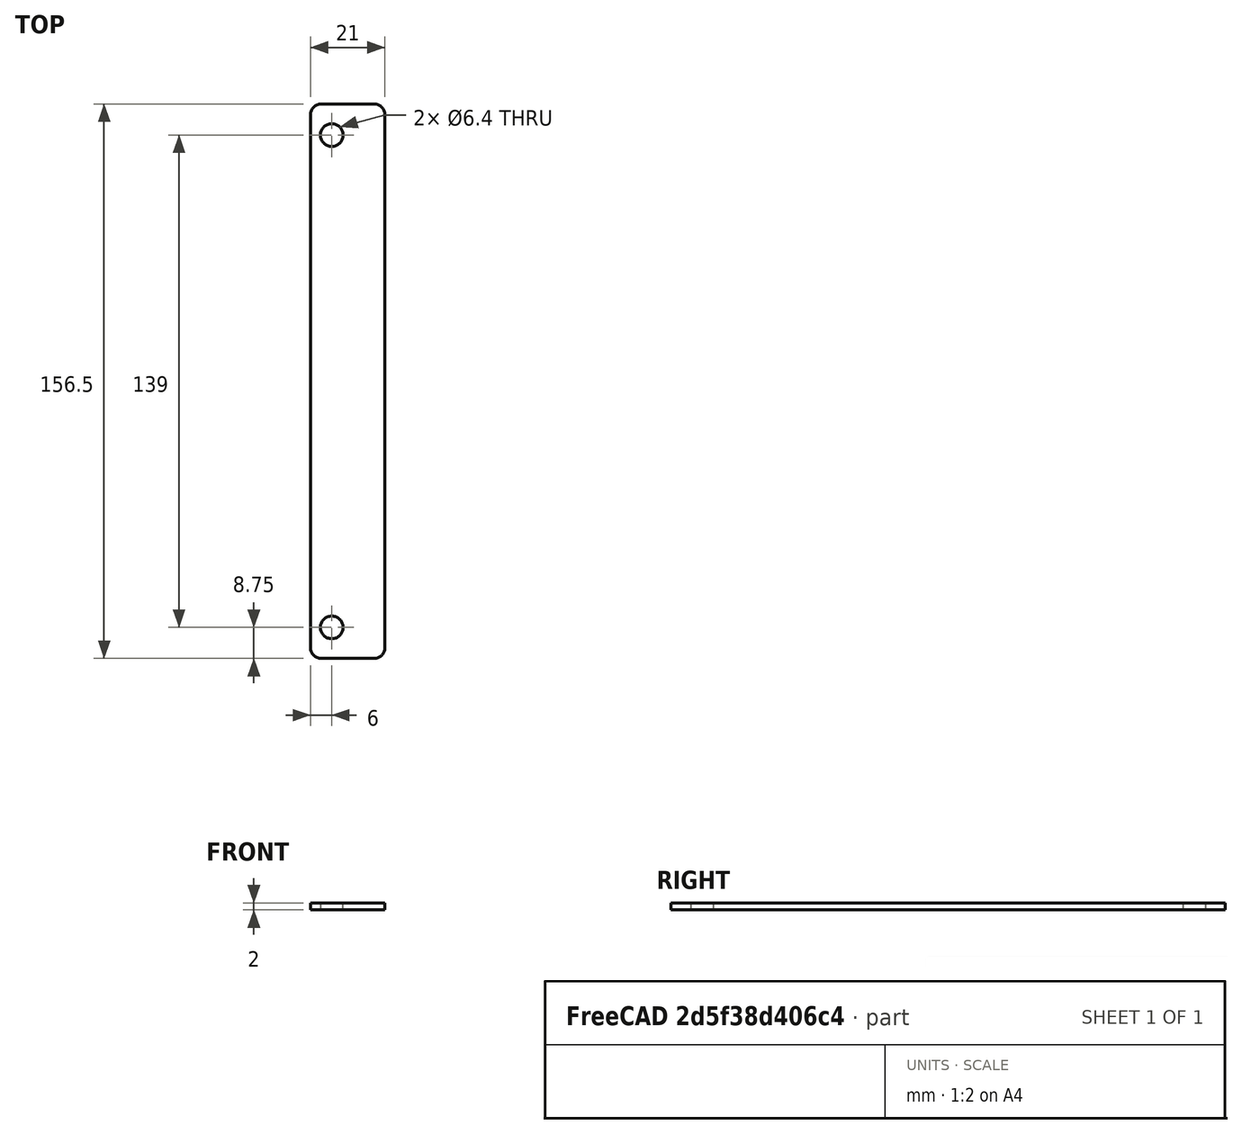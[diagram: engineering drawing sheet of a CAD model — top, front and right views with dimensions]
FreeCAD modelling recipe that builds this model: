
FCSTD DOCUMENT  (FreeCAD 0.14R2756 (Git))
Label: long_shim
License: CC-BY 3.0
LicenseURL: http://creativecommons.org/licenses/by/3.0/
objects: Sketcher::SketchObject×1, PartDesign::Pad×1
note: 3 computed .brp shape members not serialized (recipe doc carries the construction recipe); baked Part::Feature solids carry a one-line shape summary decoded from their .brp

FEATURE [Sketcher::SketchObject] Sketch
  sketch-geometry (11):
    g0: Circle CenterX=0 CenterY=0 CenterZ=0 NormalX=0 NormalY=0 NormalZ=1 Radius=3.2
    g1: Circle CenterX=0 CenterY=-139 CenterZ=0 NormalX=0 NormalY=0 NormalZ=1 Radius=3.2
    g2: LineSegment [constr] StartX=0 StartY=0 StartZ=0 EndX=0 EndY=-139 EndZ=0
    g3: LineSegment StartX=-3 StartY=8.75 StartZ=0 EndX=12 EndY=8.75 EndZ=0
    g4: LineSegment StartX=15 StartY=5.75 StartZ=0 EndX=15 EndY=-144.75 EndZ=0
    g5: LineSegment StartX=12 StartY=-147.75 StartZ=0 EndX=-3 EndY=-147.75 EndZ=0
    g6: LineSegment StartX=-6 StartY=-144.75 StartZ=0 EndX=-6 EndY=5.75 EndZ=0
    g7: ArcOfCircle CenterX=12 CenterY=5.75 CenterZ=0 NormalX=0 NormalY=0 NormalZ=1 Radius=3 StartAngle=0 EndAngle=1.5708
    g8: ArcOfCircle CenterX=-3 CenterY=5.75 CenterZ=0 NormalX=0 NormalY=0 NormalZ=1 Radius=3 StartAngle=1.5708 EndAngle=3.14159
    g9: ArcOfCircle CenterX=-3 CenterY=-144.75 CenterZ=0 NormalX=0 NormalY=0 NormalZ=1 Radius=3 StartAngle=3.14159 EndAngle=4.71239
    g10: ArcOfCircle CenterX=12 CenterY=-144.75 CenterZ=0 NormalX=0 NormalY=0 NormalZ=1 Radius=3 StartAngle=4.71239 EndAngle=6.28319
  constraints (27):
    c: Coincident(g0,g-1)
    c: Radius(g0) = 3.2
    c: Coincident(g2,g-1)
    c: Coincident(g2,g1)
    c: Vertical(g2)
    c: DistanceY(g-1,g1) = -139
    c: Equal(g1,g0)
    c: Horizontal(g3)
    c: Horizontal(g5)
    c: Vertical(g4)
    c: Vertical(g6)
    c: Tangent(g3,g7)
    c: Tangent(g4,g7)
    c: Tangent(g3,g8)
    c: Tangent(g6,g8)
    c: Tangent(g5,g9)
    c: Tangent(g6,g9)
    c: Tangent(g4,g10)
    c: Tangent(g5,g10)
    c: Radius(g8) = 3
    c: Equal(g8,g7)
    c: Equal(g8,g9)
    c: Equal(g9,g10)
    c: DistanceX(g1,g6) = -6
    c: DistanceX(g1,g4) = 15
    c: DistanceY(g1,g5) = -8.75
    c: DistanceY(g-1,g3) = 8.75
FEATURE [PartDesign::Pad] Pad
  Length = 2
  Length2 = 100
  Sketch = -> Sketch
  Type = 0
